# Revit family: CSP_v_1.01
name_source: partatom
category: Окна
revit_build: Autodesk Revit 2017 (Build: 20160225_1515(x64)
units: mm (PartAtom-declared; Revit-internal decimal feet)

## family parameters
Всегда вертикально = Нет
Общий = Нет
Основа = Крыша
При загрузке вырезать с полостями = Нет
Точка расчета площади = Нет

## types (1)
- Default
    Allowed Roof Slope = 0°-15°
    Cross Height = 85.657 мм
    Date of publishing = 6/27/2013
    Design country = Denmark
    Edition number = 1
    Emergency Exit = Нет
    Function = Smoke ventilation flat roof window
    GlazingAreaFraction = 1.57
    Height Dome = 1200 мм
    IFC Classification = Window
    Light transmittance = 0.72
    Manufacturer URL = www.velux.com
    Manufacturer country = Denmark
    Material main = Wood
    Material secondary = Glass 73Q + ISD 0000
    NBS Reference = 59-72
    NBS Reference Description = Roof Window Units
    Name of the object = Flat roof window - CSP
    Open Window = Нет
    Opening = 159.38 мм
    Operation Mode = Electrical
    Perimeter Glazing = 0
    Perimeter Window = 4.8
    Placement Height = 0 мм
    Product SKU = csp101
    Product data url = http://www.velux.dk
    Product family = Flat roof window
    Product group = CSP 1.01
    Sound Insulation db = 33
    Thermal bridge(glazing) = 0.05
    ThermalTransmittance = 1.0
    ThermalTransmittance - Glazing = 0.9
    UNSPC Category = Roofing accessories
    UNSPC code = 301516
    URL = http://file-system.ru
    Uniclass 1.4 Code = JL11
    Uniclass 1.4 Description = Rooflights/Roof windows
    Uniclass 2.0 Code = PR-59-72
    Uniclass 2.0 Description = Roof Window Units
    Warranty Years = 10
    Width Dome = 1200 мм
    Window Area = 3.78
    g-value = 0.53
    Высота = 1380 мм
    Группа модели = Flat roof window - CSP
    Изготовитель = VELUX A/S
    Код по классификатору = B3020110
    Примерная высота = 0 мм
    Примерная ширина = 0 мм
    Ширина = 1380 мм

## geometry (parser evidence)
native form markers: Blend x30, Sweep x5
no freeform markers — native parametric forms only
